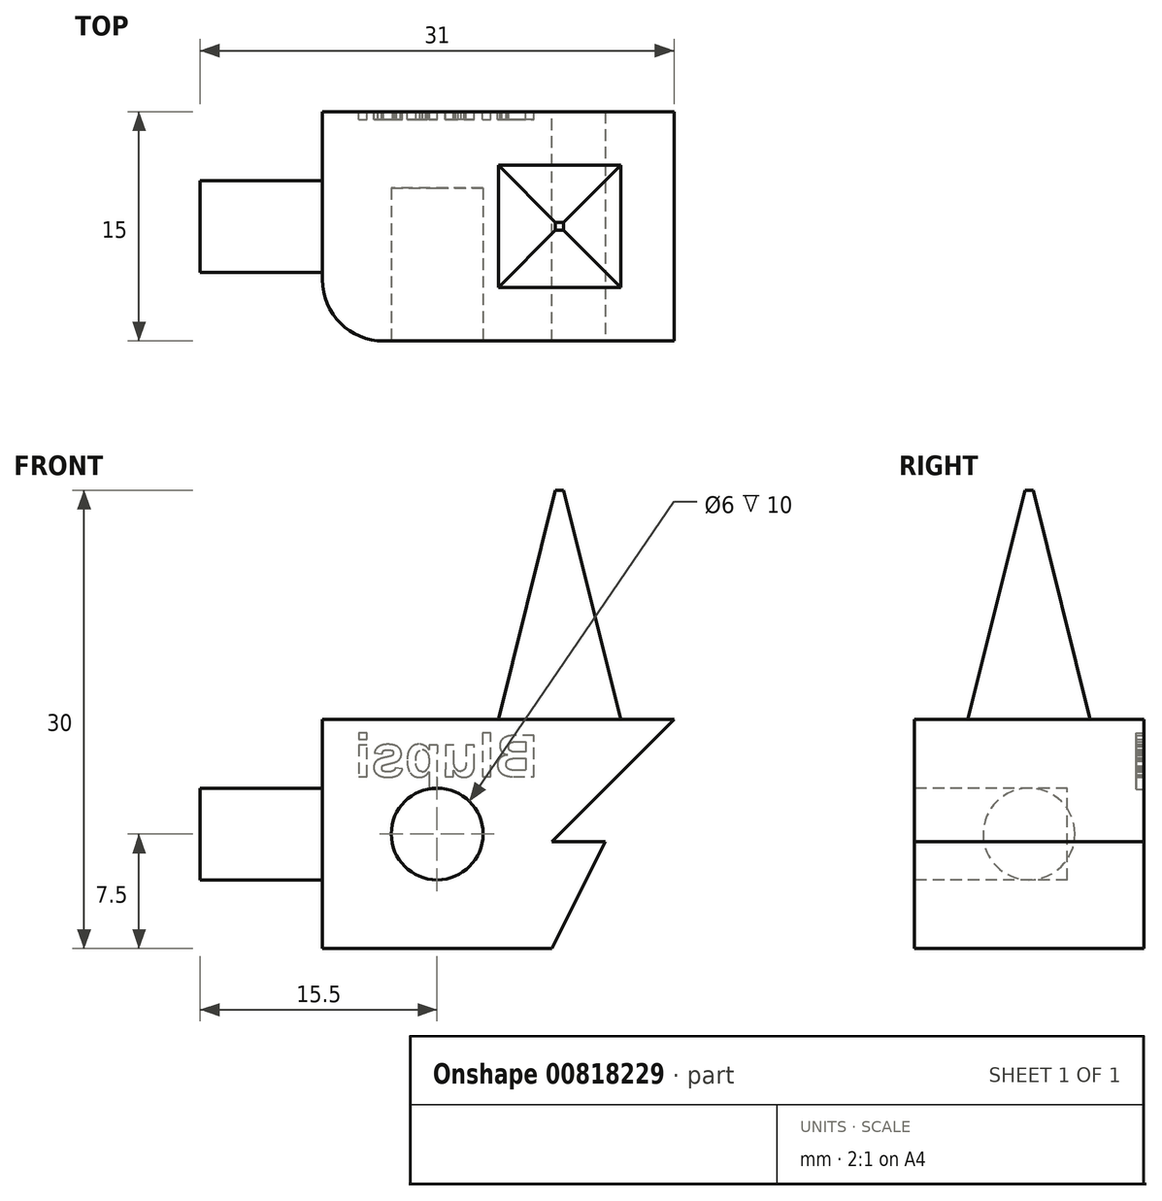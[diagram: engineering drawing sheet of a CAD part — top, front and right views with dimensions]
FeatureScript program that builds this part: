
annotation { "Feature Type Name" : "Feature", "Feature Type Description" : "" }
export const myFeature = defineFeature(function(context is Context, id is Id, definition is map)
    precondition{}
    {
        {
            var Q0;
            Q0=qCreatedBy(makeId("Front.planeOp"),FACE);
            var sketch = newSketch(context, id + "F0", { "sketchPlane" : qUnion([Q0])});
            skLineSegment(sketch, "E0.bottom", {"start": v(0, 0) * mm, "end": v(15, 0) * mm});
            skLineSegment(sketch, "E0.top", {"start": v(0, 15) * mm, "end": v(15, 15) * mm});
            skLineSegment(sketch, "E0.left", {"start": v(0, 0) * mm, "end": v(0, 15) * mm});
            skLineSegment(sketch, "E0.right", {"start": v(15, 0) * mm, "end": v(15, 15) * mm});
            skSolve(sketch);
        }
        {
            var Q0;
            Q0=makeQuery(id+"F0.imprint","IMPRINT",FACE,{"disambiguationData":[TD([[makeQuery(id+"F0.imprint","IMPRINT",EDGE,{"derivedFrom":sQuery(id+"F0.wireOp",EDGE,"E0.bottom")}),1.0]])]});
            extrude(context, id + "F1", {"entities" : qUnion([Q0]), "depth" : 15 * mm, "offsetDistance" : 25 * mm});
        }
        {
            var Q0;
            Q0=makeQuery(id+"F1.opExtrude","CAP_FACE",FACE,{"disambiguationData":[OSD([sQuery(id+"F0.wireOp",EDGE,"E0.bottom"),sQuery(id+"F0.wireOp",EDGE,"E0.top"),sQuery(id+"F0.wireOp",EDGE,"E0.left"),sQuery(id+"F0.wireOp",EDGE,"E0.right")])],"isStart":false});
            var sketch = newSketch(context, id + "F2", { "sketchPlane" : qUnion([Q0])});
            skLineSegment(sketch, "E1", {"start": v(15, 0) * mm, "end": v(18.5, 7) * mm});
            skLineSegment(sketch, "E2", {"start": v(18.5, 7) * mm, "end": v(15, 7) * mm});
            skLineSegment(sketch, "E3", {"start": v(15, 7) * mm, "end": v(15, 0) * mm});
            skLineSegment(sketch, "E4", {"start": v(15, 7) * mm, "end": v(23, 15) * mm});
            skLineSegment(sketch, "E5", {"start": v(23, 15) * mm, "end": v(15, 15) * mm});
            skLineSegment(sketch, "E6", {"start": v(15, 15) * mm, "end": v(15, 7) * mm});
            skSolve(sketch);
        }
        {
            var Q0;
            Q0 = qSketchRegion(id + "F2", true);
            var Q1;
            Q1=makeQuery(id+"F1.opExtrude","CAP_FACE",FACE,{"disambiguationData":[OSD([sQuery(id+"F0.wireOp",EDGE,"E0.bottom"),sQuery(id+"F0.wireOp",EDGE,"E0.top"),sQuery(id+"F0.wireOp",EDGE,"E0.left"),sQuery(id+"F0.wireOp",EDGE,"E0.right")])],"isStart":true});
            extrude(context, id + "F3", {"entities" : qUnion([Q0]), "operationType" : NewBodyOperationType.ADD, "endBound" : BoundingType.UP_TO_SURFACE, "oppositeDirection" : true, "depth" : 25 * mm, "endBoundEntityFace" : qUnion([Q1]), "offsetDistance" : 25 * mm});
        }
        {
            var Q0;
            Q0=makeQuery(id+"F3.boolean.opBoolean","MERGE",FACE,{"derivedFrom":[makeQuery(id+"F1.opExtrude","CAP_FACE",FACE,{"disambiguationData":[OSD([sQuery(id+"F0.wireOp",EDGE,"E0.bottom"),sQuery(id+"F0.wireOp",EDGE,"E0.top"),sQuery(id+"F0.wireOp",EDGE,"E0.left"),sQuery(id+"F0.wireOp",EDGE,"E0.right")])],"isStart":false}),makeQuery(id+"F3.opExtrude","CAP_FACE",FACE,{"disambiguationData":[OSD([sQuery(id+"F2.wireOp",EDGE,"E1"),sQuery(id+"F2.wireOp",EDGE,"E2"),sQuery(id+"F2.wireOp",EDGE,"E3")])],"isStart":true}),makeQuery(id+"F3.opExtrude","CAP_FACE",FACE,{"disambiguationData":[OSD([sQuery(id+"F2.wireOp",EDGE,"E4"),sQuery(id+"F2.wireOp",EDGE,"E5"),sQuery(id+"F2.wireOp",EDGE,"E6")])],"isStart":true})]});
            var sketch = newSketch(context, id + "F4", { "sketchPlane" : qUnion([Q0])});
            skCircle(sketch, "E7", {"center": v(7.5, 7.5) * mm, "radius": 3 * mm});
            skSolve(sketch);
        }
        {
            var Q0;
            Q0=makeQuery(id+"F4.imprint","IMPRINT",FACE,{"disambiguationData":[TD([[makeQuery(id+"F4.imprint","IMPRINT",EDGE,{"derivedFrom":sQuery(id+"F4.wireOp",EDGE,"E7")}),1.0]])]});
            extrude(context, id + "F5", {"entities" : qUnion([Q0]), "operationType" : NewBodyOperationType.REMOVE, "oppositeDirection" : true, "depth" : 10 * mm, "offsetDistance" : 25 * mm});
        }
        {
            var Q0;
            Q0=makeQuery(id+"F1.opExtrude","SWEPT_FACE",FACE,{"disambiguationData":[OSD([sQuery(id+"F0.wireOp",EDGE,"E0.left")])]});
            var sketch = newSketch(context, id + "F6", { "sketchPlane" : qUnion([Q0])});
            skCircle(sketch, "E8", {"center": v(7.5, 7.5) * mm, "radius": 3 * mm});
            skSolve(sketch);
        }
        {
            var Q0;
            Q0=makeQuery(id+"F6.imprint","IMPRINT",FACE,{"disambiguationData":[TD([[makeQuery(id+"F6.imprint","IMPRINT",EDGE,{"derivedFrom":sQuery(id+"F6.wireOp",EDGE,"E8")}),1.0]])]});
            extrude(context, id + "F7", {"entities" : qUnion([Q0]), "operationType" : NewBodyOperationType.ADD, "depth" : 8 * mm, "offsetDistance" : 25 * mm});
        }
        {
            var Q0;
            Q0=makeQuery(id+"F3.boolean.opBoolean","MERGE",FACE,{"derivedFrom":[makeQuery(id+"F1.opExtrude","SWEPT_FACE",FACE,{"disambiguationData":[OSD([sQuery(id+"F0.wireOp",EDGE,"E0.top")])]}),makeQuery(id+"F3.opExtrude","SWEPT_FACE",FACE,{"disambiguationData":[OSD([sQuery(id+"F2.wireOp",EDGE,"E5")])]})]});
            var sketch = newSketch(context, id + "F8", { "sketchPlane" : qUnion([Q0])});
            skLineSegment(sketch, "E9.bottom", {"start": v(19.5, -11.5) * mm, "end": v(11.5, -11.5) * mm});
            skLineSegment(sketch, "E9.top", {"start": v(19.5, -3.5) * mm, "end": v(11.5, -3.5) * mm});
            skLineSegment(sketch, "E9.left", {"start": v(19.5, -11.5) * mm, "end": v(19.5, -3.5) * mm});
            skLineSegment(sketch, "E9.right", {"start": v(11.5, -11.5) * mm, "end": v(11.5, -3.5) * mm});
            skPoint(sketch, "E9.middle", {"position": v(15.5, -7.5) * mm});
            skSolve(sketch);
        }
        {
            var Q0;
            Q0=makeQuery(id+"F8.imprint","IMPRINT",FACE,{"disambiguationData":[TD([[makeQuery(id+"F8.imprint","IMPRINT",EDGE,{"derivedFrom":sQuery(id+"F8.wireOp",EDGE,"E9.bottom")}),-1.0]])]});
            extrude(context, id + "F9", {"entities" : qUnion([Q0]), "operationType" : NewBodyOperationType.ADD, "depth" : 15 * mm, "offsetDistance" : 25 * mm, "hasDraft" : true, "draftAngle" : 14 * degree, "draftPullDirection" : true});
        }
        {
            var Q0;
            Q0=makeQuery(id+"F1.opExtrude","CAP_EDGE",EDGE,{"disambiguationData":[OSD([sQuery(id+"F0.wireOp",EDGE,"E0.left")])],"isStart":false});
            fillet(context, id + "F10", {"entities" : qUnion([Q0]), "radius" : 4 * mm, "tangentPropagation" : true, "allowEdgeOverflow" : false});
        }
        {
            var Q0;
            {var subQ0=sQuery(id+"F0.wireOp",EDGE,"E0.right");var subQ1=sQuery(id+"F0.wireOp",EDGE,"E0.left");var subQ2=sQuery(id+"F0.wireOp",EDGE,"E0.top");var subQ3=sQuery(id+"F0.wireOp",EDGE,"E0.bottom");Q0=makeQuery(id+"F3.boolean.opBoolean","MERGE",FACE,{"derivedFrom":[makeQuery(id+"F1.opExtrude","CAP_FACE",FACE,{"disambiguationData":[OSD([subQ3,subQ2,subQ1,subQ0])],"isStart":true}),makeQuery(id+"F3.opExtrude","CAP_FACE",FACE,{"disambiguationData":[OSD([subQ3,subQ2,subQ1,subQ0]),OD(0.0)],"isStart":false}),makeQuery(id+"F3.opExtrude","CAP_FACE",FACE,{"disambiguationData":[OSD([subQ3,subQ2,subQ1,subQ0]),OD(1.0)],"isStart":false})]});}
            var sketch = newSketch(context, id + "F11", { "sketchPlane" : qUnion([Q0])});
            skText(sketch, "E10", { "text": "Blupsi", "fontName": "Arimo-Bold.ttf"});
            const initialGuessF11  = {"E10": [-0.01411, 0.01125, 1, 0, 0.00283]};
            skSetInitialGuess(sketch, initialGuessF11);
            skSolve(sketch);
        }
        {
            var Q0;
            Q0 = qSketchRegion(id + "F11", true);
            extrude(context, id + "F12", {"entities" : qUnion([Q0]), "operationType" : NewBodyOperationType.REMOVE, "oppositeDirection" : true, "depth" : 0.5 * mm, "offsetDistance" : 25 * mm});
        }
    });
